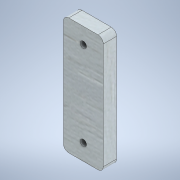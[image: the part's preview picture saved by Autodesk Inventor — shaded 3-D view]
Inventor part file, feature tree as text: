
AUTODESK INVENTOR PART (.ipt)
format: ipt  version: 2021 (Build 250183000, 183)  size: 124,928 bytes
history: native  units: mm
features: extrude x2, sketch x2
ambient origin geometry x8: Origin, YZ Plane, XZ Plane, XY Plane, X Axis, Y Axis, Z Axis, Center Point
bodies: Solid1 (feature_tree)
feature tree (4):
  extrude  "Extrusion1"  Depth=5.0mm
  extrude  "Extrusion2"  Depth=10.0mm
  sketch  "Sketch1"  dims[d0=5.0mm d1=0.0mm d2=2.4mm]
  sketch  "Sketch2"  dims[d3=7.5mm d4=2.4mm d5=10.0mm d6=0.0mm]
